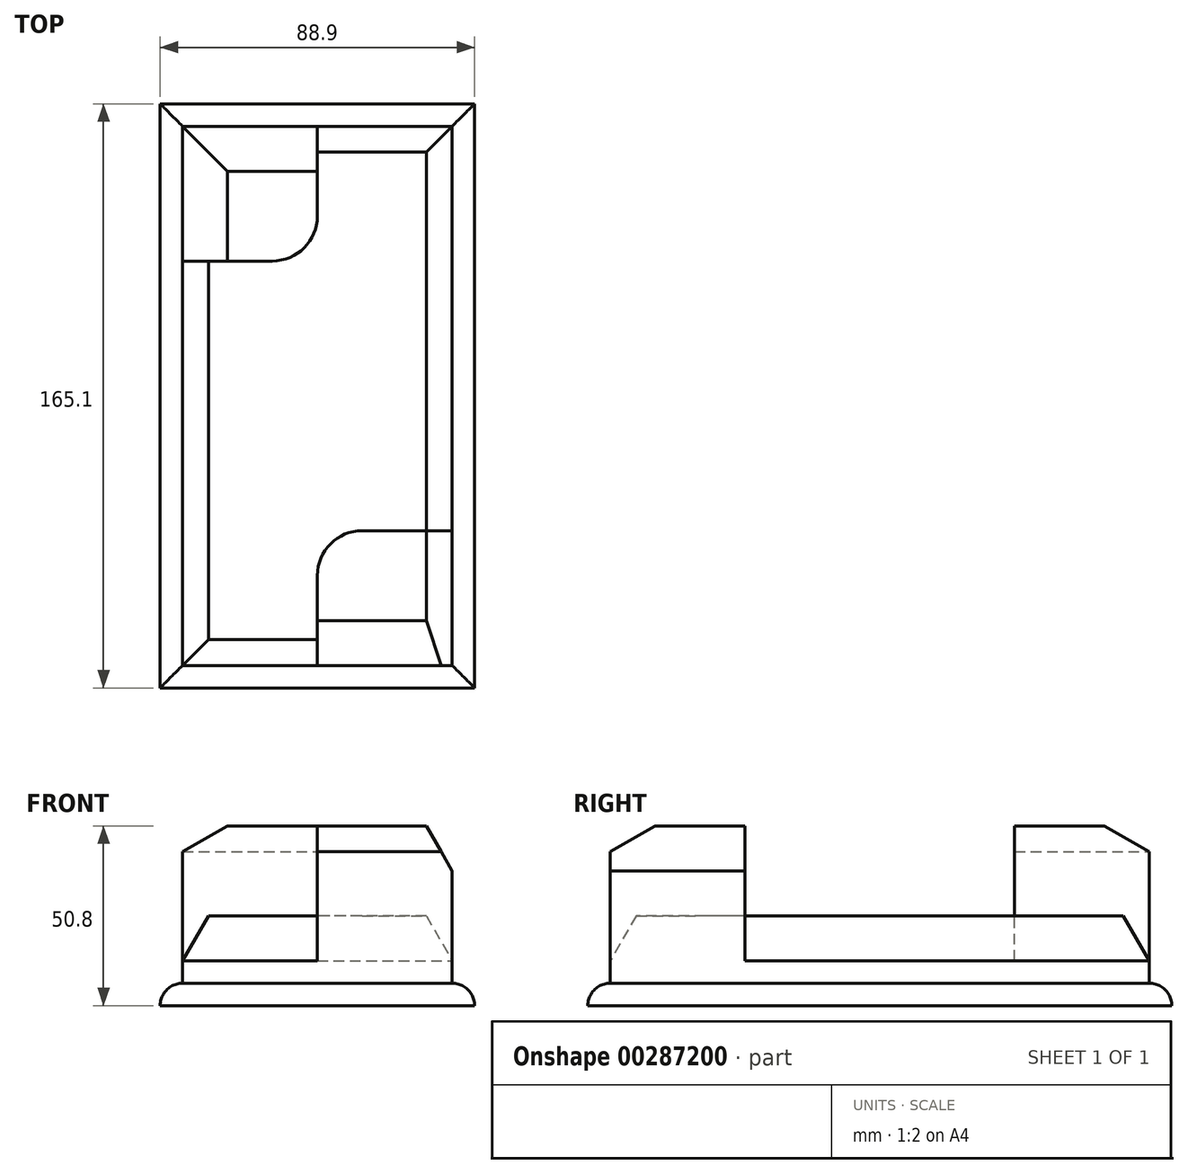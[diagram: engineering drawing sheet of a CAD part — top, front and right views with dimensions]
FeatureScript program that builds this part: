
annotation { "Feature Type Name" : "Feature", "Feature Type Description" : "" }
export const myFeature = defineFeature(function(context is Context, id is Id, definition is map)
    precondition{}
    {
        {
            var Q0;
            Q0=qCreatedBy(makeId("Top.planeOp"),FACE);
            var sketch = newSketch(context, id + "F0", { "sketchPlane" : qUnion([Q0])});
            skPoint(sketch, "E0.middle", {"position": v(0, 0) * mm});
            skLineSegment(sketch, "E1.bottom", {"start": v(-38.1, 76.2) * mm, "end": v(38.1, 76.2) * mm});
            skLineSegment(sketch, "E1.top", {"start": v(-38.1, -76.2) * mm, "end": v(38.1, -76.2) * mm});
            skLineSegment(sketch, "E1.left", {"start": v(-38.1, 76.2) * mm, "end": v(-38.1, -76.2) * mm});
            skLineSegment(sketch, "E1.right", {"start": v(38.1, 76.2) * mm, "end": v(38.1, -76.2) * mm});
            skLineSegment(sketch, "E2", {"start": v(0, 76.2) * mm, "end": v(0, 50.8) * mm});
            skPoint(sketch, "E2.endSnap0", {"position": v(0, 76.2) * mm});
            skLineSegment(sketch, "E3", {"start": v(-12.7, 38.1) * mm, "end": v(-38.1, 38.1) * mm});
            skLineSegment(sketch, "E4", {"start": v(0, -76.2) * mm, "end": v(0, -50.8) * mm});
            skPoint(sketch, "E4.endSnap0", {"position": v(0, -76.2) * mm});
            skLineSegment(sketch, "E5", {"start": v(12.7, -38.1) * mm, "end": v(38.1, -38.1) * mm});
            skPoint(sketch, "E6.visualSharp", {"position": v(0, 38.1) * mm});
            skArc(sketch, "E6.filletArc", {"start": v(-12.7, 38.1) * mm, "mid": v(-3.72, 41.82) * mm, "end": v(0, 50.8) * mm});
            skPoint(sketch, "E7.visualSharp", {"position": v(0, -38.1) * mm});
            skArc(sketch, "E7.filletArc", {"start": v(12.7, -38.1) * mm, "mid": v(3.72, -41.82) * mm, "end": v(0, -50.8) * mm});
            skLineSegment(sketch, "E8.0", {"start": v(-44.45, -82.55) * mm, "end": v(44.45, -82.55) * mm});
            skLineSegment(sketch, "E8.1", {"start": v(-44.45, 82.55) * mm, "end": v(-44.45, -82.55) * mm});
            skLineSegment(sketch, "E8.2", {"start": v(-44.45, 82.55) * mm, "end": v(44.45, 82.55) * mm});
            skLineSegment(sketch, "E8.3", {"start": v(44.45, 82.55) * mm, "end": v(44.45, -82.55) * mm});
            skSolve(sketch);
        }
        {
            var Q0;
            Q0=makeQuery(id+"F0.imprint","IMPRINT",FACE,{"disambiguationData":[TD([[makeQuery(id+"F0.imprint","IMPRINT",EDGE,{"derivedFrom":sQuery(id+"F0.wireOp",EDGE,"E8.0")}),1.0]])]});
            extrude(context, id + "F1", {"entities" : qUnion([Q0]), "depth" : 6.35 * mm});
        }
        {
            var Q0;
            {var subQ9=sQuery(id+"F0.wireOp",EDGE,"E2");Q0=makeQuery(id+"F0.imprint","IMPRINT",FACE,{"disambiguationData":[TD([[makeQuery(id+"F0.imprint","IMPRINT",EDGE,{"derivedFrom":subQ9}),1.0]])]});}
            extrude(context, id + "F2", {"entities" : qUnion([Q0]), "operationType" : NewBodyOperationType.ADD, "depth" : 25.4 * mm});
        }
        {
            var Q0;
            {var subQ1=sQuery(id+"F0.wireOp",EDGE,"E4");Q0=makeQuery(id+"F0.imprint","IMPRINT",FACE,{"disambiguationData":[TD([[makeQuery(id+"F0.imprint","IMPRINT",EDGE,{"derivedFrom":subQ1}),-1.0]])]});}
            var Q1;
            {var subQ0=sQuery(id+"F0.wireOp",EDGE,"E2");Q1=makeQuery(id+"F0.imprint","IMPRINT",FACE,{"disambiguationData":[TD([[makeQuery(id+"F0.imprint","IMPRINT",EDGE,{"derivedFrom":subQ0}),-1.0]])]});}
            extrude(context, id + "F3", {"entities" : qUnion([Q0, Q1]), "operationType" : NewBodyOperationType.ADD, "depth" : 50.8 * mm});
        }
        {
            var Q0;
            Q0=makeQuery(id+"F1.opExtrude","CAP_EDGE",EDGE,{"disambiguationData":[OSD([sQuery(id+"F0.wireOp",EDGE,"E8.0")])],"isStart":false});
            var Q1;
            Q1=makeQuery(id+"F1.opExtrude","CAP_EDGE",EDGE,{"disambiguationData":[OSD([sQuery(id+"F0.wireOp",EDGE,"E8.3")])],"isStart":false});
            var Q2;
            Q2=makeQuery(id+"F1.opExtrude","CAP_EDGE",EDGE,{"disambiguationData":[OSD([sQuery(id+"F0.wireOp",EDGE,"E8.2")])],"isStart":false});
            var Q3;
            Q3=makeQuery(id+"F1.opExtrude","CAP_EDGE",EDGE,{"disambiguationData":[OSD([sQuery(id+"F0.wireOp",EDGE,"E8.1")])],"isStart":false});
            fillet(context, id + "F4", {"entities" : qUnion([Q0, Q1, Q2, Q3]), "radius" : 6.35 * mm, "tangentPropagation" : true, "allowEdgeOverflow" : false});
        }
        {
            var Q0;
            Q0=makeQuery(id+"F2.opExtrude","CAP_EDGE",EDGE,{"disambiguationData":[OSD([sQuery(id+"F0.wireOp",EDGE,"E1.right")])],"isStart":false});
            var Q1;
            Q1=makeQuery(id+"F3.opExtrude","CAP_EDGE",EDGE,{"disambiguationData":[OSD([sQuery(id+"F0.wireOp",EDGE,"E1.right")])],"isStart":false});
            var Q2;
            Q2=makeQuery(id+"F3.opExtrude","CAP_EDGE",EDGE,{"disambiguationData":[OSD([sQuery(id+"F0.wireOp",EDGE,"E1.top")])],"isStart":false});
            var Q3;
            Q3=makeQuery(id+"F2.opExtrude","CAP_EDGE",EDGE,{"disambiguationData":[OSD([sQuery(id+"F0.wireOp",EDGE,"E1.bottom")])],"isStart":false});
            var Q4;
            Q4=makeQuery(id+"F3.opExtrude","CAP_EDGE",EDGE,{"disambiguationData":[OSD([sQuery(id+"F0.wireOp",EDGE,"E1.left")])],"isStart":false});
            var Q5;
            Q5=makeQuery(id+"F2.opExtrude","CAP_EDGE",EDGE,{"disambiguationData":[OSD([sQuery(id+"F0.wireOp",EDGE,"E1.left")])],"isStart":false});
            var Q6;
            Q6=makeQuery(id+"F2.opExtrude","CAP_EDGE",EDGE,{"disambiguationData":[OSD([sQuery(id+"F0.wireOp",EDGE,"E1.top")])],"isStart":false});
            chamfer(context, id + "F5", {"entities" : qUnion([Q0, Q1, Q2, Q3, Q4, Q5, Q6]), "chamferType" : ChamferType.OFFSET_ANGLE, "width" : 12.7 * mm, "oppositeDirection" : false, "angle" : 30 * degree, "tangentPropagation" : true});
        }
        {
            var Q0;
            Q0=makeQuery(id+"F3.opExtrude","CAP_EDGE",EDGE,{"disambiguationData":[OSD([sQuery(id+"F0.wireOp",EDGE,"E1.bottom")])],"isStart":false});
            chamfer(context, id + "F6", {"entities" : qUnion([Q0]), "chamferType" : ChamferType.OFFSET_ANGLE, "width" : 12.7 * mm, "oppositeDirection" : true, "angle" : 30 * degree, "tangentPropagation" : true});
        }
    });
